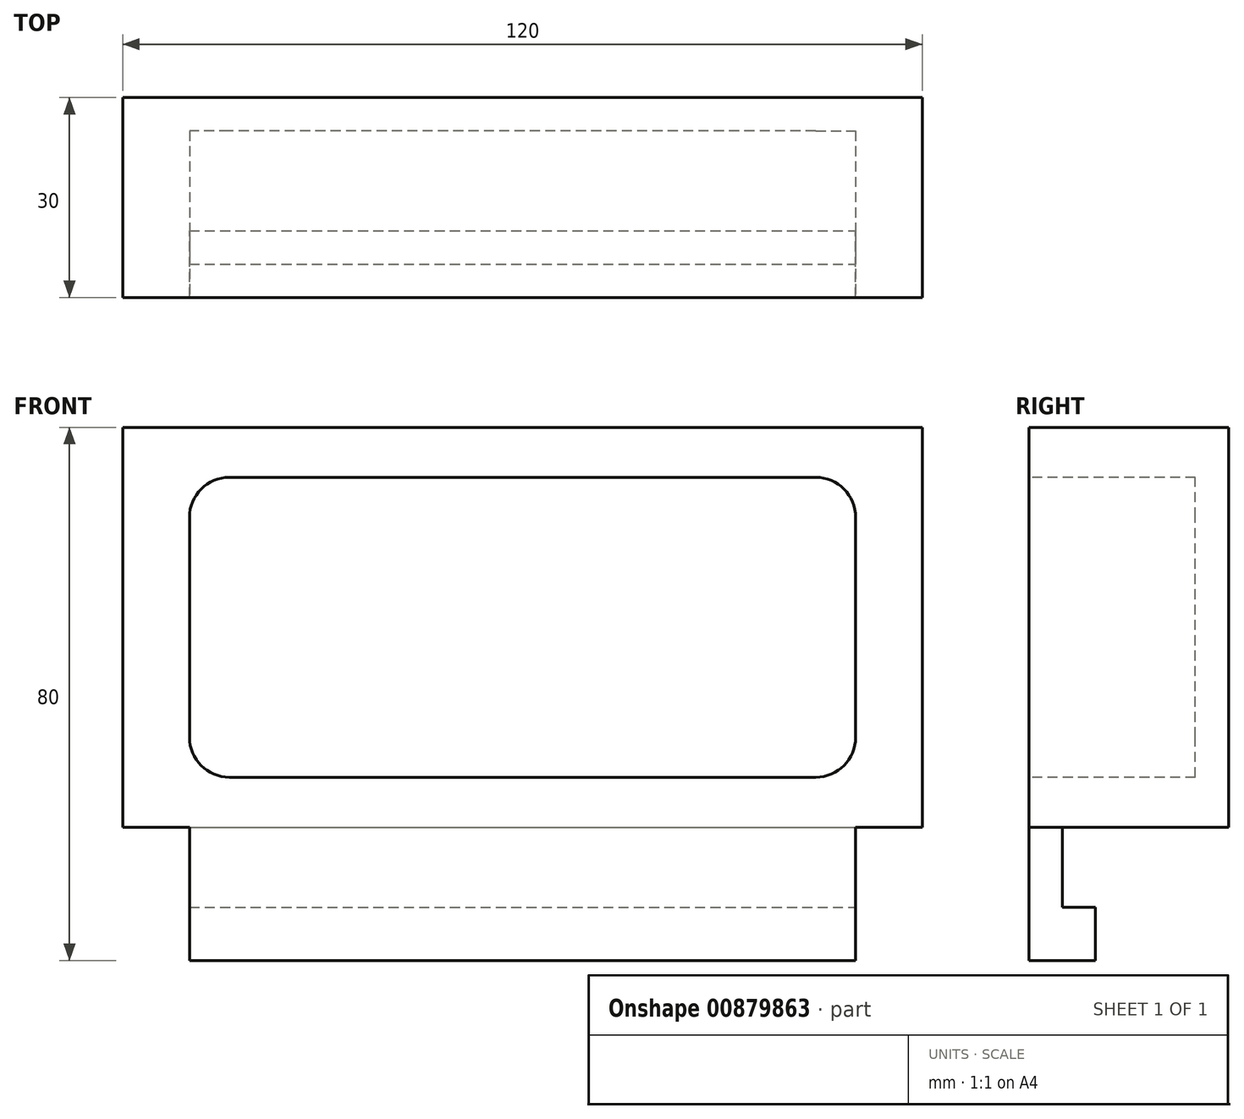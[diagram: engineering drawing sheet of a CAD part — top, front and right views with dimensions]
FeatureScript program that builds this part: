
annotation { "Feature Type Name" : "Feature", "Feature Type Description" : "" }
export const myFeature = defineFeature(function(context is Context, id is Id, definition is map)
    precondition{}
    {
        {
            var Q0;
            Q0=qCreatedBy(makeId("Front.planeOp"),FACE);
            var sketch = newSketch(context, id + "F0", { "sketchPlane" : qUnion([Q0])});
            skLineSegment(sketch, "E0.bottom", {"start": v(50, 110) * mm, "end": v(170, 110) * mm});
            skLineSegment(sketch, "E0.top", {"start": v(50, 50) * mm, "end": v(170, 50) * mm});
            skLineSegment(sketch, "E0.left", {"start": v(50, 110) * mm, "end": v(50, 50) * mm});
            skLineSegment(sketch, "E0.right", {"start": v(170, 110) * mm, "end": v(170, 50) * mm});
            skSolve(sketch);
        }
        {
            var Q0;
            Q0 = qSketchRegion(id + "F0", true);
            extrude(context, id + "F1", {"entities" : qUnion([Q0]), "depth" : 30 * mm, "offsetDistance" : 25 * mm});
        }
        {
            var Q0;
            Q0=makeQuery(id+"F1.opExtrude","CAP_FACE",FACE,{"disambiguationData":[OSD([sQuery(id+"F0.wireOp",EDGE,"E0.bottom"),sQuery(id+"F0.wireOp",EDGE,"E0.top"),sQuery(id+"F0.wireOp",EDGE,"E0.left"),sQuery(id+"F0.wireOp",EDGE,"E0.right")])],"isStart":false});
            var sketch = newSketch(context, id + "F2", { "sketchPlane" : qUnion([Q0])});
            skLineSegment(sketch, "E1.bottom", {"start": v(154, 57.5) * mm, "end": v(66, 57.5) * mm});
            skLineSegment(sketch, "E1.top", {"start": v(154, 102.5) * mm, "end": v(66, 102.5) * mm});
            skLineSegment(sketch, "E1.left", {"start": v(160, 63.5) * mm, "end": v(160, 96.5) * mm});
            skLineSegment(sketch, "E1.right", {"start": v(60, 63.5) * mm, "end": v(60, 96.5) * mm});
            skPoint(sketch, "E1.middle", {"position": v(110, 80) * mm});
            skPoint(sketch, "E2.visualSharp", {"position": v(160, 102.5) * mm});
            skArc(sketch, "E2.filletArc", {"start": v(160, 96.5) * mm, "mid": v(158.24, 100.74) * mm, "end": v(154, 102.5) * mm});
            skPoint(sketch, "E3.visualSharp", {"position": v(160, 57.5) * mm});
            skArc(sketch, "E3.filletArc", {"start": v(154, 57.5) * mm, "mid": v(158.24, 59.26) * mm, "end": v(160, 63.5) * mm});
            skPoint(sketch, "E4.visualSharp", {"position": v(60, 57.5) * mm});
            skArc(sketch, "E4.filletArc", {"start": v(60, 63.5) * mm, "mid": v(61.76, 59.26) * mm, "end": v(66, 57.5) * mm});
            skPoint(sketch, "E5.visualSharp", {"position": v(60, 102.5) * mm});
            skArc(sketch, "E5.filletArc", {"start": v(66, 102.5) * mm, "mid": v(61.76, 100.74) * mm, "end": v(60, 96.5) * mm});
            skSolve(sketch);
        }
        {
            var Q0;
            Q0 = qSketchRegion(id + "F2", true);
            extrude(context, id + "F3", {"entities" : qUnion([Q0]), "operationType" : NewBodyOperationType.REMOVE, "oppositeDirection" : true, "depth" : 25 * mm, "offsetDistance" : 25 * mm});
        }
        {
            var Q0;
            Q0=makeQuery(id+"F1.opExtrude","SWEPT_FACE",FACE,{"disambiguationData":[OSD([sQuery(id+"F0.wireOp",EDGE,"E0.top")])]});
            var sketch = newSketch(context, id + "F4", { "sketchPlane" : qUnion([Q0])});
            skLineSegment(sketch, "E6.bottom", {"start": v(160, 30) * mm, "end": v(60, 30) * mm});
            skLineSegment(sketch, "E6.top", {"start": v(160, 20) * mm, "end": v(60, 20) * mm});
            skLineSegment(sketch, "E6.left", {"start": v(160, 30) * mm, "end": v(160, 20) * mm});
            skLineSegment(sketch, "E6.right", {"start": v(60, 30) * mm, "end": v(60, 20) * mm});
            skSolve(sketch);
        }
        {
            var Q0;
            Q0 = qSketchRegion(id + "F4", true);
            extrude(context, id + "F5", {"entities" : qUnion([Q0]), "operationType" : NewBodyOperationType.ADD, "depth" : 20 * mm, "offsetDistance" : 25 * mm});
        }
        {
            var Q0;
            Q0=makeQuery(id+"F5.opExtrude","SWEPT_FACE",FACE,{"disambiguationData":[OSD([sQuery(id+"F4.wireOp",EDGE,"E6.left")])]});
            var sketch = newSketch(context, id + "F6", { "sketchPlane" : qUnion([Q0])});
            skLineSegment(sketch, "E7.bottom", {"start": v(-20, 50) * mm, "end": v(-25, 50) * mm});
            skLineSegment(sketch, "E7.top", {"start": v(-20, 38) * mm, "end": v(-25, 38) * mm});
            skLineSegment(sketch, "E7.left", {"start": v(-20, 50) * mm, "end": v(-20, 38) * mm});
            skLineSegment(sketch, "E7.right", {"start": v(-25, 50) * mm, "end": v(-25, 38) * mm});
            skSolve(sketch);
        }
        {
            var Q0;
            Q0 = qSketchRegion(id + "F6", true);
            extrude(context, id + "F7", {"entities" : qUnion([Q0]), "operationType" : NewBodyOperationType.REMOVE, "endBound" : BoundingType.THROUGH_ALL, "oppositeDirection" : true, "depth" : 25 * mm, "offsetDistance" : 25 * mm});
        }
    });
